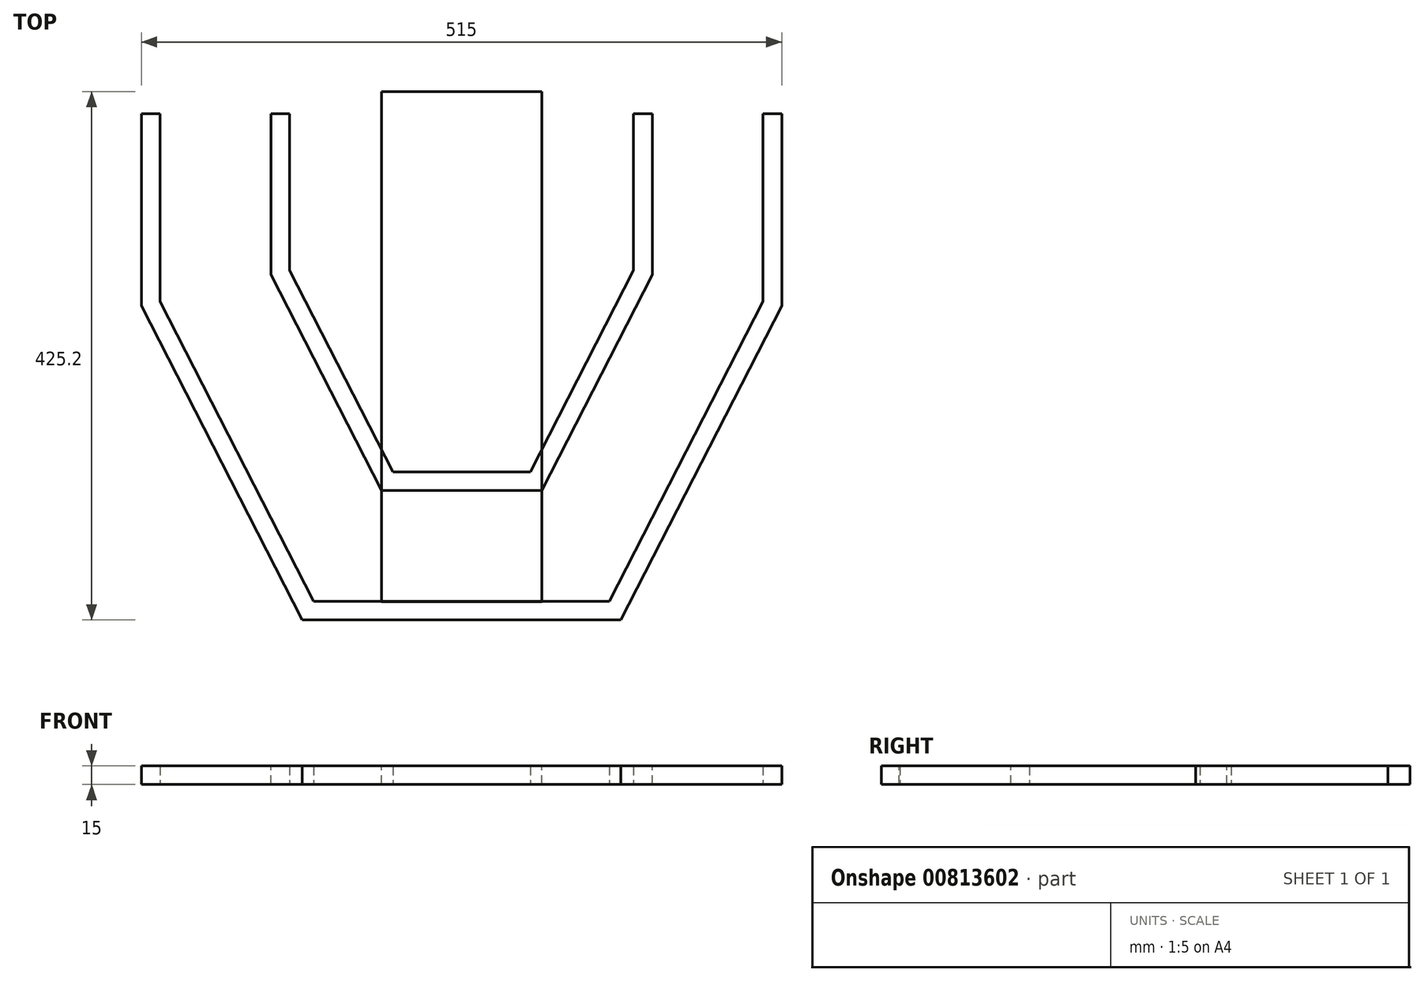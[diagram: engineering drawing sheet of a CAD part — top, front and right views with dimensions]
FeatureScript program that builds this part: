
annotation { "Feature Type Name" : "Feature", "Feature Type Description" : "" }
export const myFeature = defineFeature(function(context is Context, id is Id, definition is map)
    precondition{}
    {
        {
            var Q0;
            Q0=qCreatedBy(makeId("Top.planeOp"),FACE);
            var sketch = newSketch(context, id + "F0", { "sketchPlane" : qUnion([Q0])});
            skLineSegment(sketch, "E0", {"start": v(0, 0) * mm, "end": v(-145.86, 0) * mm});
            skLineSegment(sketch, "E1", {"start": v(0, -400) * mm, "end": v(0, -1900) * mm});
            skLineSegment(sketch, "E2", {"start": v(-229.17, -1900) * mm, "end": v(236.46, -1900) * mm});
            skLineSegment(sketch, "E3", {"start": v(-145.86, 0) * mm, "end": v(-250, 0) * mm});
            skLineSegment(sketch, "E4.MirrorCS", {"start": v(0, 0) * mm, "end": v(145.86, 0) * mm});
            skLineSegment(sketch, "E5.MirrorCS", {"start": v(145.86, 0) * mm, "end": v(250, 0) * mm});
            skLineSegment(sketch, "E6", {"start": v(-123.53, -400) * mm, "end": v(0, -400) * mm});
            skLineSegment(sketch, "E7.MirrorCS", {"start": v(123.53, -400) * mm, "end": v(0, -400) * mm});
            skLineSegment(sketch, "E8", {"start": v(-250, 0) * mm, "end": v(-250, -152.95) * mm});
            skLineSegment(sketch, "E9", {"start": v(-250, -152.95) * mm, "end": v(-123.53, -400) * mm});
            skLineSegment(sketch, "E10", {"start": v(123.53, -400) * mm, "end": v(250, -152.95) * mm});
            skLineSegment(sketch, "E11", {"start": v(250, -152.95) * mm, "end": v(250, 0) * mm});
            skSolve(sketch);
        }
        {
            var Q0;
            Q0=qCreatedBy(makeId("Front.planeOp"),FACE);
            var sketch = newSketch(context, id + "F1", { "sketchPlane" : qUnion([Q0])});
            skLineSegment(sketch, "E12.bottom", {"start": v(-138.36, 7.5) * mm, "end": v(-153.36, 7.5) * mm});
            skLineSegment(sketch, "E12.top", {"start": v(-138.36, -7.5) * mm, "end": v(-153.36, -7.5) * mm});
            skLineSegment(sketch, "E12.left", {"start": v(-138.36, 7.5) * mm, "end": v(-138.36, -7.5) * mm});
            skLineSegment(sketch, "E12.right", {"start": v(-153.36, 7.5) * mm, "end": v(-153.36, -7.5) * mm});
            skPoint(sketch, "E12.middle", {"position": v(-145.86, 0) * mm});
            skLineSegment(sketch, "E13.bottom", {"start": v(-242.5, 7.5) * mm, "end": v(-257.5, 7.5) * mm});
            skLineSegment(sketch, "E13.top", {"start": v(-242.5, -7.5) * mm, "end": v(-257.5, -7.5) * mm});
            skLineSegment(sketch, "E13.left", {"start": v(-242.5, 7.5) * mm, "end": v(-242.5, -7.5) * mm});
            skLineSegment(sketch, "E13.right", {"start": v(-257.5, 7.5) * mm, "end": v(-257.5, -7.5) * mm});
            skPoint(sketch, "E13.middle", {"position": v(-250, 0) * mm});
            skLineSegment(sketch, "E14.MirrorCS", {"start": v(138.36, -7.5) * mm, "end": v(153.36, -7.5) * mm});
            skLineSegment(sketch, "E15.MirrorCS", {"start": v(242.5, 7.5) * mm, "end": v(257.5, 7.5) * mm});
            skLineSegment(sketch, "E16.MirrorCS", {"start": v(153.36, 7.5) * mm, "end": v(153.36, -7.5) * mm});
            skLineSegment(sketch, "E17.MirrorCS", {"start": v(138.36, 7.5) * mm, "end": v(138.36, -7.5) * mm});
            skLineSegment(sketch, "E18.MirrorCS", {"start": v(242.5, 7.5) * mm, "end": v(242.5, -7.5) * mm});
            skLineSegment(sketch, "E19.MirrorCS", {"start": v(138.36, 7.5) * mm, "end": v(153.36, 7.5) * mm});
            skLineSegment(sketch, "E20.MirrorCS", {"start": v(257.5, 7.5) * mm, "end": v(257.5, -7.5) * mm});
            skLineSegment(sketch, "E21.MirrorCS", {"start": v(242.5, -7.5) * mm, "end": v(257.5, -7.5) * mm});
            skPoint(sketch, "E22.MirrorP", {"position": v(250, 0) * mm});
            skPoint(sketch, "E23.MirrorP", {"position": v(145.86, 0) * mm});
            skSolve(sketch);
        }
        {
            var Q0;
            Q0=makeQuery(id+"F1.imprint","IMPRINT",FACE,{"disambiguationData":[TD([[makeQuery(id+"F1.imprint","IMPRINT",EDGE,{"derivedFrom":sQuery(id+"F1.wireOp",EDGE,"E13.bottom")}),1.0]])]});
            var Q1;
            Q1=makeQuery(id+"F1.imprint","IMPRINT",FACE,{"disambiguationData":[TD([[makeQuery(id+"F1.imprint","IMPRINT",EDGE,{"derivedFrom":sQuery(id+"F1.wireOp",EDGE,"E12.bottom")}),1.0]])]});
            var Q2;
            Q2=sQuery(id+"F0.wireOp",EDGE,"E8");
            var Q3;
            Q3=sQuery(id+"F0.wireOp",EDGE,"E9");
            var Q4;
            Q4=sQuery(id+"F0.wireOp",EDGE,"E6");
            var Q5;
            Q5=sQuery(id+"F0.wireOp",EDGE,"E7.MirrorCS");
            var Q6;
            Q6=sQuery(id+"F0.wireOp",EDGE,"E10");
            var Q7;
            Q7=sQuery(id+"F0.wireOp",EDGE,"E11");
            sweep(context, id + "F2", {"profiles" : qUnion([Q0, Q1]), "path" : qUnion([Q2, Q3, Q4, Q5, Q6, Q7])});
        }
        {
            var Q0;
            Q0=makeQuery(id+"F2.opSweep","SWEPT_FACE",FACE,{"disambiguationData":[OSD([sQuery(id+"F0.wireOp",EDGE,"E7.MirrorCS"),sQuery(id+"F1.wireOp",EDGE,"E12.right")])]});
            extrude(context, id + "F3", {"entities" : qUnion([Q0]), "depth" : 89.66 * mm, "offsetDistance" : 25.4 * mm, "hasSecondDirection" : true, "secondDirectionOppositeDirection" : true, "secondDirectionDepth" : 321.06 * mm});
        }
    });
